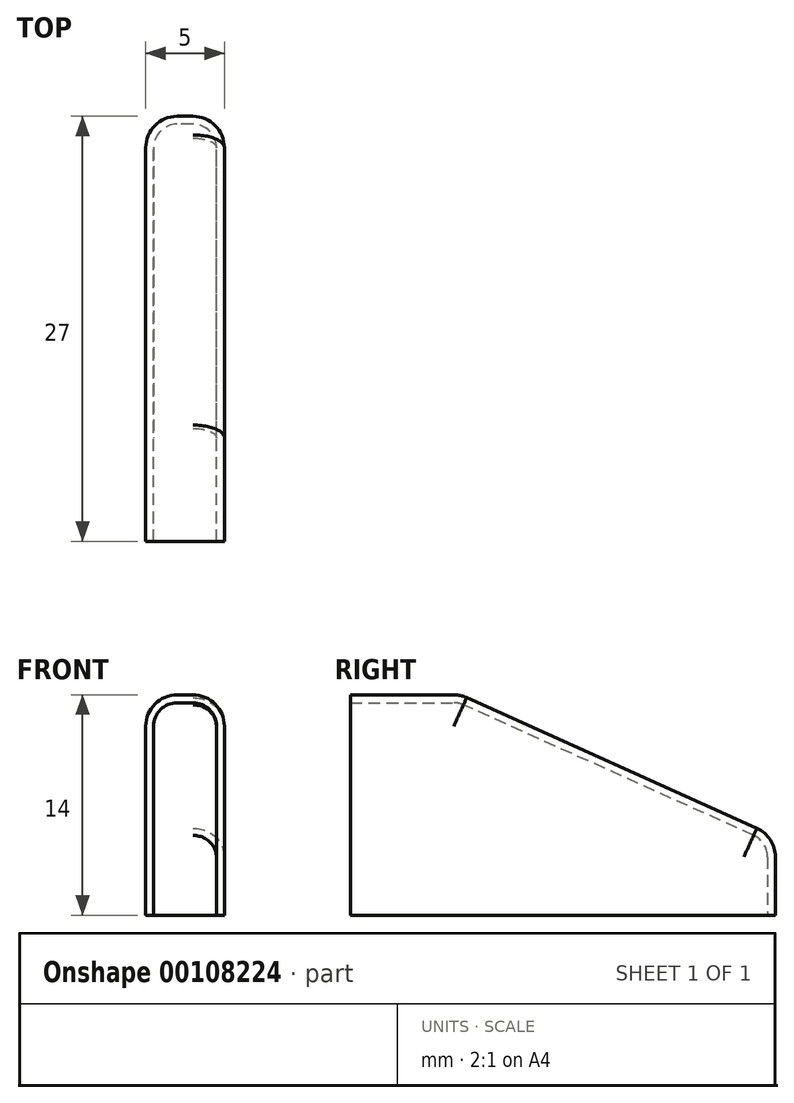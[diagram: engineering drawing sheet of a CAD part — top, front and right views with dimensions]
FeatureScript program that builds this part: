
annotation { "Feature Type Name" : "Feature", "Feature Type Description" : "" }
export const myFeature = defineFeature(function(context is Context, id is Id, definition is map)
    precondition{}
    {
        {
            var Q0;
            Q0=qCreatedBy(makeId("Right.planeOp"),FACE);
            var sketch = newSketch(context, id + "F0", { "sketchPlane" : qUnion([Q0])});
            skLineSegment(sketch, "E0", {"start": v(-59.88, -33.43) * mm, "end": v(-32.88, -33.43) * mm});
            skLineSegment(sketch, "E1", {"start": v(-32.88, -33.43) * mm, "end": v(-32.88, -28.43) * mm});
            skLineSegment(sketch, "E2", {"start": v(-59.88, -33.43) * mm, "end": v(-59.88, -19.43) * mm});
            skLineSegment(sketch, "E3", {"start": v(-59.88, -19.43) * mm, "end": v(-52.88, -19.43) * mm});
            skLineSegment(sketch, "E4", {"start": v(-52.88, -19.43) * mm, "end": v(-32.88, -28.43) * mm});
            skSolve(sketch);
        }
        {
            var Q0;
            Q0 = qSketchRegion(id + "F0", true);
            extrude(context, id + "F1", {"entities" : qUnion([Q0]), "endBound" : BoundingType.SYMMETRIC, "depth" : 5 * mm});
        }
        {
            var Q0;
            Q0=makeQuery(id+"F1.opExtrude","CAP_EDGE",EDGE,{"disambiguationData":[OSD([sQuery(id+"F0.wireOp",EDGE,"E4")])],"isStart":false});
            fillet(context, id + "F2", {"entities" : qUnion([Q0]), "radius" : 2 * mm, "tangentPropagation" : true, "allowEdgeOverflow" : false});
        }
        {
            var Q0;
            Q0=makeQuery(id+"F1.opExtrude","CAP_EDGE",EDGE,{"disambiguationData":[OSD([sQuery(id+"F0.wireOp",EDGE,"E3")])],"isStart":false});
            var Q1;
            Q1=makeQuery(id+"F1.opExtrude","CAP_EDGE",EDGE,{"disambiguationData":[OSD([sQuery(id+"F0.wireOp",EDGE,"E1")])],"isStart":false});
            fillet(context, id + "F3", {"entities" : qUnion([Q0, Q1]), "radius" : 2 * mm, "tangentPropagation" : true, "allowEdgeOverflow" : false});
        }
        {
            var Q0;
            Q0=makeQuery(id+"F1.opExtrude","CAP_EDGE",EDGE,{"disambiguationData":[OSD([sQuery(id+"F0.wireOp",EDGE,"E4")])],"isStart":true});
            fillet(context, id + "F4", {"entities" : qUnion([Q0]), "radius" : 2 * mm, "tangentPropagation" : true, "allowEdgeOverflow" : false});
        }
        {
            var Q0;
            Q0=makeQuery(id+"F1.opExtrude","SWEPT_FACE",FACE,{"disambiguationData":[OSD([sQuery(id+"F0.wireOp",EDGE,"E0")])]});
            var Q1;
            Q1=makeQuery(id+"F1.opExtrude","SWEPT_FACE",FACE,{"disambiguationData":[OSD([sQuery(id+"F0.wireOp",EDGE,"E2")])]});
            shell(context, id + "F5", {"entities" : qUnion([Q0, Q1]), "thickness" : 0.5 * mm});
        }
    });
